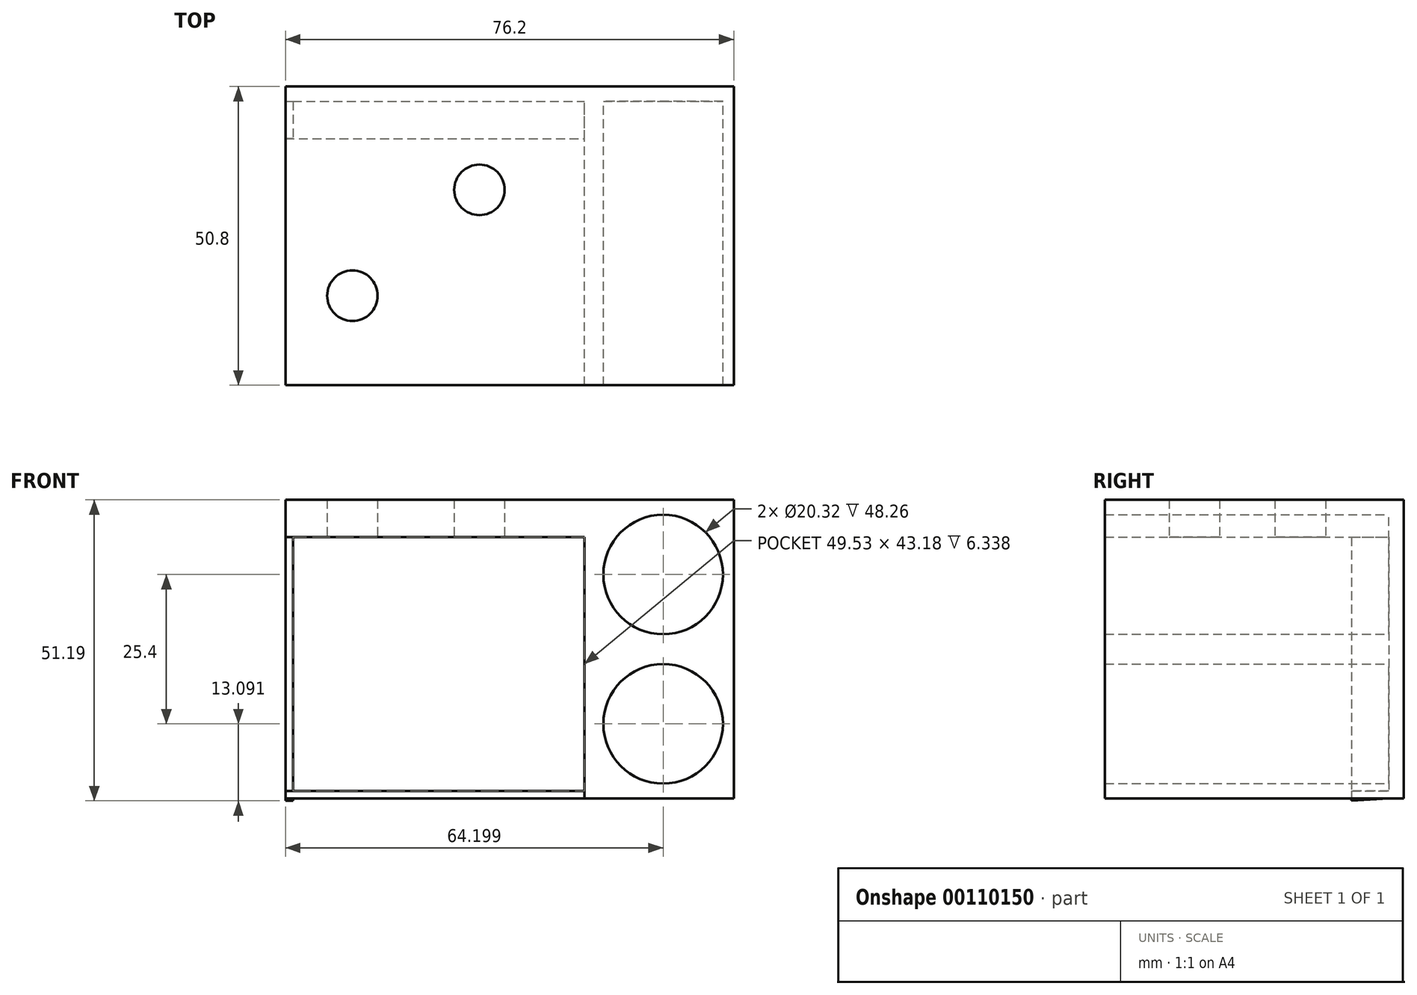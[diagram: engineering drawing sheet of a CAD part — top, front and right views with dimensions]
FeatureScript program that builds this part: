
annotation { "Feature Type Name" : "Feature", "Feature Type Description" : "" }
export const myFeature = defineFeature(function(context is Context, id is Id, definition is map)
    precondition{}
    {
        {
            var Q0;
            Q0=qCreatedBy(makeId("Front.planeOp"),FACE);
            var sketch = newSketch(context, id + "F0", { "sketchPlane" : qUnion([Q0])});
            skLineSegment(sketch, "E0", {"start": v(-56.22, 18.75) * mm, "end": v(-56.22, -32.05) * mm});
            skLineSegment(sketch, "E1", {"start": v(-56.22, -32.05) * mm, "end": v(19.98, -32.05) * mm});
            skLineSegment(sketch, "E2", {"start": v(19.98, -32.05) * mm, "end": v(19.98, 18.75) * mm});
            skLineSegment(sketch, "E3", {"start": v(19.98, 18.75) * mm, "end": v(-56.22, 18.75) * mm});
            skLineSegment(sketch, "E4", {"start": v(-56.22, 12.4) * mm, "end": v(-5.42, 12.4) * mm});
            skLineSegment(sketch, "E5", {"start": v(-5.42, 12.4) * mm, "end": v(-5.42, -32.05) * mm});
            skCircle(sketch, "E6", {"center": v(7.98, -19.35) * mm, "radius": 10.16 * mm});
            skCircle(sketch, "E7", {"center": v(7.98, 6.05) * mm, "radius": 10.16 * mm});
            skSolve(sketch);
        }
        {
            var Q0;
            {var subQ1=sQuery(id+"F0.wireOp",EDGE,"E2");Q0=makeQuery(id+"F0.imprint","IMPRINT",FACE,{"disambiguationData":[TD([[makeQuery(id+"F0.imprint","IMPRINT",EDGE,{"derivedFrom":subQ1}),1.0]])]});}
            extrude(context, id + "F1", {"entities" : qUnion([Q0]), "depth" : 50.8 * mm});
        }
        {
            var Q0;
            {var subQ3=sQuery(id+"F0.wireOp",EDGE,"E4");Q0=makeQuery(id+"F0.imprint","IMPRINT",FACE,{"disambiguationData":[TD([[makeQuery(id+"F0.imprint","IMPRINT",EDGE,{"derivedFrom":subQ3}),-1.0]])]});}
            var Q1;
            Q1=makeQuery(id+"F0.imprint","IMPRINT",FACE,{"disambiguationData":[TD([[makeQuery(id+"F0.imprint","IMPRINT",EDGE,{"derivedFrom":sQuery(id+"F0.wireOp",EDGE,"E6")}),1.0]])]});
            var Q2;
            Q2=makeQuery(id+"F0.imprint","IMPRINT",FACE,{"disambiguationData":[TD([[makeQuery(id+"F0.imprint","IMPRINT",EDGE,{"derivedFrom":sQuery(id+"F0.wireOp",EDGE,"E7")}),1.0]])]});
            extrude(context, id + "F2", {"entities" : qUnion([Q0, Q1, Q2]), "operationType" : NewBodyOperationType.ADD, "depth" : 2.54 * mm});
        }
        {
            var Q0;
            {var subQ0=sQuery(id+"F0.wireOp",EDGE,"E1");Q0=makeQuery(id+"F2.boolean.opBoolean","MERGE",FACE,{"derivedFrom":[makeQuery(id+"F1.opExtrude","SWEPT_FACE",FACE,{"disambiguationData":[OSD([subQ0])]}),makeQuery(id+"F2.opExtrude","SWEPT_FACE",FACE,{"disambiguationData":[OSD([subQ0])]})]});}
            var sketch = newSketch(context, id + "F3", { "sketchPlane" : qUnion([Q0])});
            skLineSegment(sketch, "E8", {"start": v(-56.22, 2.54) * mm, "end": v(-56.22, 8.9) * mm});
            skLineSegment(sketch, "E9", {"start": v(-56.22, 8.9) * mm, "end": v(-5.42, 8.9) * mm});
            skLineSegment(sketch, "E10", {"start": v(-5.42, 8.9) * mm, "end": v(-5.42, 2.54) * mm});
            skLineSegment(sketch, "E11", {"start": v(-5.42, 2.54) * mm, "end": v(-56.22, 2.54) * mm});
            skSolve(sketch);
        }
        {
            var Q0;
            {var subQ0=sQuery(id+"F0.wireOp",EDGE,"E0");Q0=makeQuery(id+"F2.boolean.opBoolean","MERGE",FACE,{"derivedFrom":[makeQuery(id+"F1.opExtrude","SWEPT_FACE",FACE,{"disambiguationData":[OSD([subQ0])]}),makeQuery(id+"F2.opExtrude","SWEPT_FACE",FACE,{"disambiguationData":[OSD([subQ0])]})]});}
            var sketch = newSketch(context, id + "F4", { "sketchPlane" : qUnion([Q0])});
            skLineSegment(sketch, "E12", {"start": v(2.54, 12.4) * mm, "end": v(8.88, 12.4) * mm});
            skLineSegment(sketch, "E13", {"start": v(8.88, 12.4) * mm, "end": v(8.88, -32.44) * mm});
            skLineSegment(sketch, "E14", {"start": v(8.88, -32.44) * mm, "end": v(2.54, -32.05) * mm});
            skLineSegment(sketch, "E15", {"start": v(2.54, -32.05) * mm, "end": v(2.54, 12.4) * mm});
            skSolve(sketch);
        }
        {
            var Q0;
            Q0=makeQuery(id+"F4.imprint","IMPRINT",FACE,{"disambiguationData":[TD([[makeQuery(id+"F4.imprint","IMPRINT",EDGE,{"derivedFrom":sQuery(id+"F4.wireOp",EDGE,"E12")}),1.0]])]});
            extrude(context, id + "F5", {"entities" : qUnion([Q0]), "operationType" : NewBodyOperationType.ADD, "oppositeDirection" : true, "depth" : 1.27 * mm});
        }
        {
            var Q0;
            Q0=makeQuery(id+"F3.imprint","IMPRINT",FACE,{"disambiguationData":[TD([[makeQuery(id+"F3.imprint","IMPRINT",EDGE,{"derivedFrom":sQuery(id+"F3.wireOp",EDGE,"E8")}),-1.0]])]});
            extrude(context, id + "F6", {"entities" : qUnion([Q0]), "operationType" : NewBodyOperationType.ADD, "oppositeDirection" : true, "depth" : 1.27 * mm});
        }
        {
            var Q0;
            Q0=makeQuery(id+"F1.opExtrude","SWEPT_FACE",FACE,{"disambiguationData":[OSD([sQuery(id+"F0.wireOp",EDGE,"E4")])]});
            var sketch = newSketch(context, id + "F7", { "sketchPlane" : qUnion([Q0])});
            skCircle(sketch, "E16", {"center": v(-44.83, 35.59) * mm, "radius": 4.3 * mm});
            skCircle(sketch, "E17", {"center": v(-23.24, 17.58) * mm, "radius": 4.3 * mm});
            skSolve(sketch);
        }
        {
            var Q0;
            Q0=makeQuery(id+"F7.imprint","IMPRINT",FACE,{"disambiguationData":[TD([[makeQuery(id+"F7.imprint","IMPRINT",EDGE,{"derivedFrom":sQuery(id+"F7.wireOp",EDGE,"E16")}),1.0]])]});
            var Q1;
            Q1=makeQuery(id+"F7.imprint","IMPRINT",FACE,{"disambiguationData":[TD([[makeQuery(id+"F7.imprint","IMPRINT",EDGE,{"derivedFrom":sQuery(id+"F7.wireOp",EDGE,"E17")}),1.0]])]});
            extrude(context, id + "F8", {"entities" : qUnion([Q0, Q1]), "operationType" : NewBodyOperationType.REMOVE, "endBound" : BoundingType.THROUGH_ALL, "oppositeDirection" : true, "depth" : 25.4 * mm});
        }
    });
